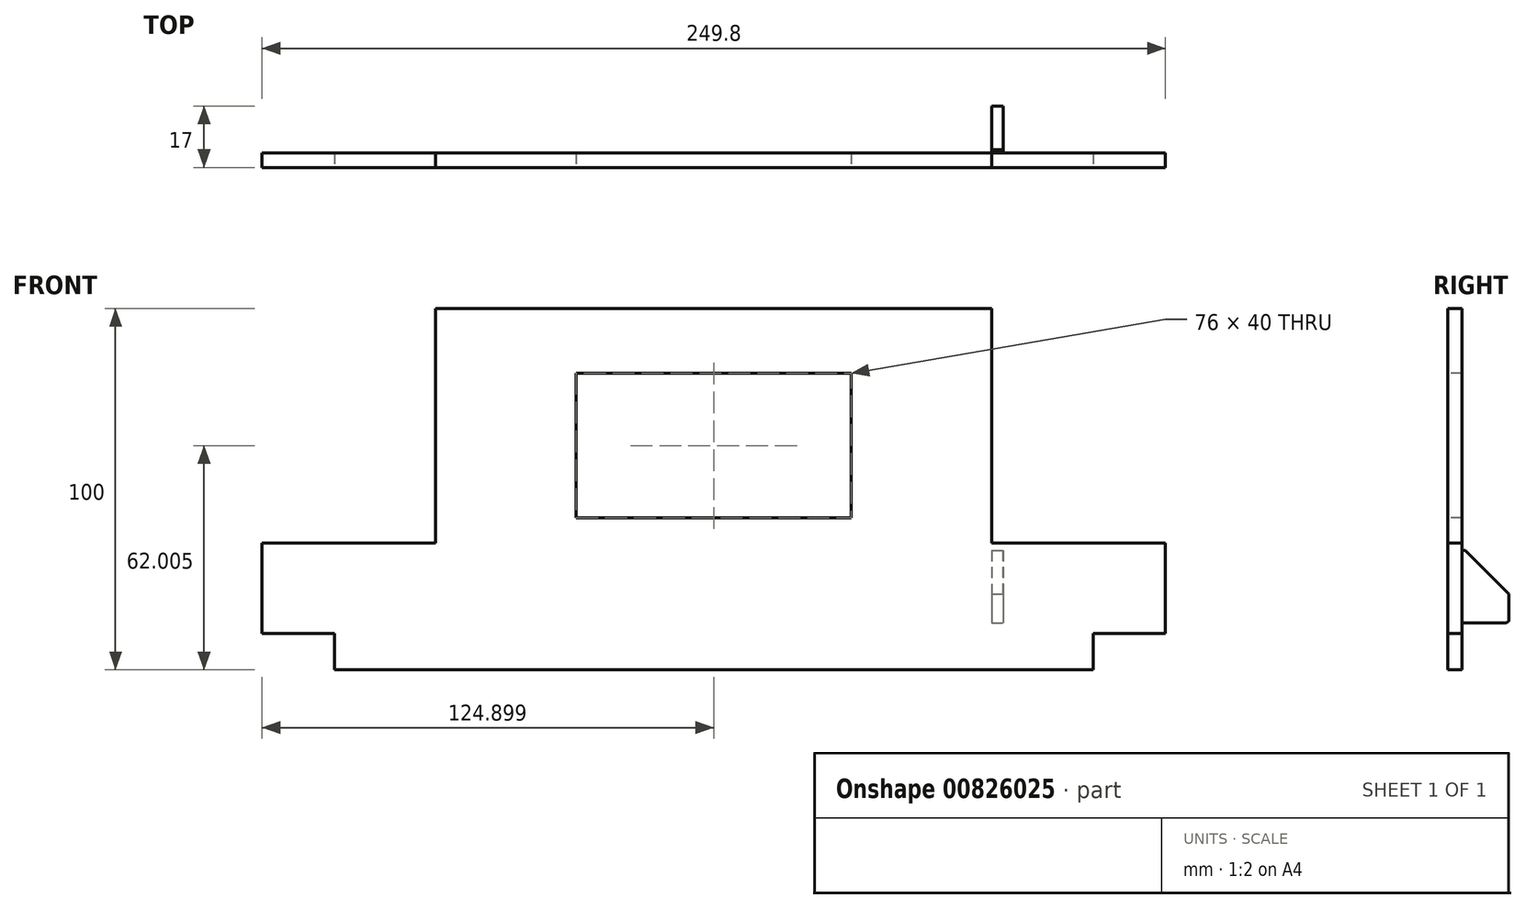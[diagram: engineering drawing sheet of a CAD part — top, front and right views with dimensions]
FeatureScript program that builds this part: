
annotation { "Feature Type Name" : "Feature", "Feature Type Description" : "" }
export const myFeature = defineFeature(function(context is Context, id is Id, definition is map)
    precondition{}
    {
        {
            var Q0;
            Q0=qCreatedBy(makeId("Front.planeOp"),FACE);
            var sketch = newSketch(context, id + "F0", { "sketchPlane" : qUnion([Q0])});
            skLineSegment(sketch, "E0.bottom", {"start": v(-79.6, 59.58) * mm, "end": v(170.2, 59.58) * mm});
            skLineSegment(sketch, "E0.top", {"start": v(-79.6, -40.42) * mm, "end": v(170.2, -40.42) * mm});
            skLineSegment(sketch, "E0.left", {"start": v(-79.6, 59.58) * mm, "end": v(-79.6, -40.42) * mm});
            skLineSegment(sketch, "E0.right", {"start": v(170.2, 59.58) * mm, "end": v(170.2, -40.42) * mm});
            skSolve(sketch);
        }
        {
            var Q0;
            Q0 = qSketchRegion(id + "F0", true);
            extrude(context, id + "F1", {"entities" : qUnion([Q0]), "depth" : 4 * mm, "offsetDistance" : 25 * mm});
        }
        {
            var Q0;
            Q0=makeQuery(id+"F1.opExtrude","CAP_FACE",FACE,{"disambiguationData":[OSD([sQuery(id+"F0.wireOp",EDGE,"E0.bottom"),sQuery(id+"F0.wireOp",EDGE,"E0.top"),sQuery(id+"F0.wireOp",EDGE,"E0.left"),sQuery(id+"F0.wireOp",EDGE,"E0.right")])],"isStart":false});
            var sketch = newSketch(context, id + "F2", { "sketchPlane" : qUnion([Q0])});
            skLineSegment(sketch, "E1.bottom", {"start": v(170.2, -40.42) * mm, "end": v(150.2, -40.42) * mm});
            skLineSegment(sketch, "E1.top", {"start": v(170.2, -30.42) * mm, "end": v(150.2, -30.42) * mm});
            skLineSegment(sketch, "E1.left", {"start": v(170.2, -40.42) * mm, "end": v(170.2, -30.42) * mm});
            skLineSegment(sketch, "E1.right", {"start": v(150.2, -40.42) * mm, "end": v(150.2, -30.42) * mm});
            skLineSegment(sketch, "E2.bottom", {"start": v(-79.6, -40.42) * mm, "end": v(-59.6, -40.42) * mm});
            skLineSegment(sketch, "E2.top", {"start": v(-79.6, -30.42) * mm, "end": v(-59.6, -30.42) * mm});
            skLineSegment(sketch, "E2.left", {"start": v(-79.6, -40.42) * mm, "end": v(-79.6, -30.42) * mm});
            skLineSegment(sketch, "E2.right", {"start": v(-59.6, -40.42) * mm, "end": v(-59.6, -30.42) * mm});
            skSolve(sketch);
        }
        {
            var Q0;
            Q0 = qSketchRegion(id + "F2", true);
            extrude(context, id + "F3", {"entities" : qUnion([Q0]), "operationType" : NewBodyOperationType.REMOVE, "oppositeDirection" : true, "depth" : 25 * mm, "offsetDistance" : 25 * mm});
        }
        {
            var Q0;
            Q0=makeQuery(id+"F1.opExtrude","CAP_FACE",FACE,{"disambiguationData":[OSD([sQuery(id+"F0.wireOp",EDGE,"E0.bottom"),sQuery(id+"F0.wireOp",EDGE,"E0.top"),sQuery(id+"F0.wireOp",EDGE,"E0.left"),sQuery(id+"F0.wireOp",EDGE,"E0.right")])],"isStart":false});
            var sketch = newSketch(context, id + "F4", { "sketchPlane" : qUnion([Q0])});
            skLineSegment(sketch, "E3", {"start": v(45.3, -40.42) * mm, "end": v(45.3, 59.58) * mm, "construction": true});
            skLineSegment(sketch, "E4.bottom", {"start": v(83.3, 1.58) * mm, "end": v(7.3, 1.58) * mm});
            skLineSegment(sketch, "E4.top", {"start": v(83.3, 41.58) * mm, "end": v(7.3, 41.58) * mm});
            skLineSegment(sketch, "E4.left", {"start": v(83.3, 1.58) * mm, "end": v(83.3, 41.58) * mm});
            skLineSegment(sketch, "E4.right", {"start": v(7.3, 1.58) * mm, "end": v(7.3, 41.58) * mm});
            skPoint(sketch, "E4.middle", {"position": v(45.3, 21.58) * mm});
            skLineSegment(sketch, "E5.bottom", {"start": v(-79.6, 59.58) * mm, "end": v(-31.6, 59.58) * mm});
            skLineSegment(sketch, "E5.top", {"start": v(-79.6, -5.42) * mm, "end": v(-31.6, -5.42) * mm});
            skLineSegment(sketch, "E5.left", {"start": v(-79.6, 59.58) * mm, "end": v(-79.6, -5.42) * mm});
            skLineSegment(sketch, "E5.right", {"start": v(-31.6, 59.58) * mm, "end": v(-31.6, -5.42) * mm});
            skLineSegment(sketch, "E6.MirrorCS", {"start": v(170.2, -5.42) * mm, "end": v(122.2, -5.42) * mm});
            skLineSegment(sketch, "E7.MirrorCS", {"start": v(170.2, 59.58) * mm, "end": v(170.2, -5.42) * mm});
            skLineSegment(sketch, "E8.MirrorCS", {"start": v(122.2, 59.58) * mm, "end": v(122.2, -5.42) * mm});
            skLineSegment(sketch, "E9.MirrorCS", {"start": v(170.2, 59.58) * mm, "end": v(122.2, 59.58) * mm});
            skSolve(sketch);
        }
        {
            var Q0;
            Q0 = qSketchRegion(id + "F4", true);
            extrude(context, id + "F5", {"entities" : qUnion([Q0]), "operationType" : NewBodyOperationType.REMOVE, "oppositeDirection" : true, "depth" : 25 * mm, "offsetDistance" : 25 * mm});
        }
        {
            var Q0;
            Q0=makeQuery(id+"F1.opExtrude","CAP_FACE",FACE,{"disambiguationData":[OSD([sQuery(id+"F0.wireOp",EDGE,"E0.bottom"),sQuery(id+"F0.wireOp",EDGE,"E0.top"),sQuery(id+"F0.wireOp",EDGE,"E0.left"),sQuery(id+"F0.wireOp",EDGE,"E0.right")])],"isStart":true});
            var sketch = newSketch(context, id + "F6", { "sketchPlane" : qUnion([Q0])});
            skLineSegment(sketch, "E10.bottom", {"start": v(-122.2, -7.42) * mm, "end": v(-125.4, -7.42) * mm});
            skLineSegment(sketch, "E10.top", {"start": v(-122.2, -27.42) * mm, "end": v(-125.4, -27.42) * mm});
            skLineSegment(sketch, "E10.left", {"start": v(-122.2, -7.42) * mm, "end": v(-122.2, -27.42) * mm});
            skLineSegment(sketch, "E10.right", {"start": v(-125.4, -7.42) * mm, "end": v(-125.4, -27.42) * mm});
            skSolve(sketch);
        }
        {
            var Q0;
            Q0 = qSketchRegion(id + "F6", true);
            extrude(context, id + "F7", {"entities" : qUnion([Q0]), "operationType" : NewBodyOperationType.ADD, "depth" : 13 * mm, "offsetDistance" : 25 * mm});
        }
        {
            var Q0;
            Q0=makeQuery(id+"F7.opExtrude","CAP_EDGE",EDGE,{"disambiguationData":[OSD([sQuery(id+"F6.wireOp",EDGE,"E10.bottom")])],"isStart":false});
            chamfer(context, id + "F8", {"entities" : qUnion([Q0]), "width" : 12.1 * mm, "tangentPropagation" : true});
        }
        {
            var Q0;
            Q0=makeQuery(id+"F7.opExtrude","CAP_EDGE",EDGE,{"disambiguationData":[OSD([sQuery(id+"F6.wireOp",EDGE,"E10.top")])],"isStart":false});
            fillet(context, id + "F9", {"entities" : qUnion([Q0]), "radius" : 1 * mm, "tangentPropagation" : true, "allowEdgeOverflow" : false});
        }
    });
